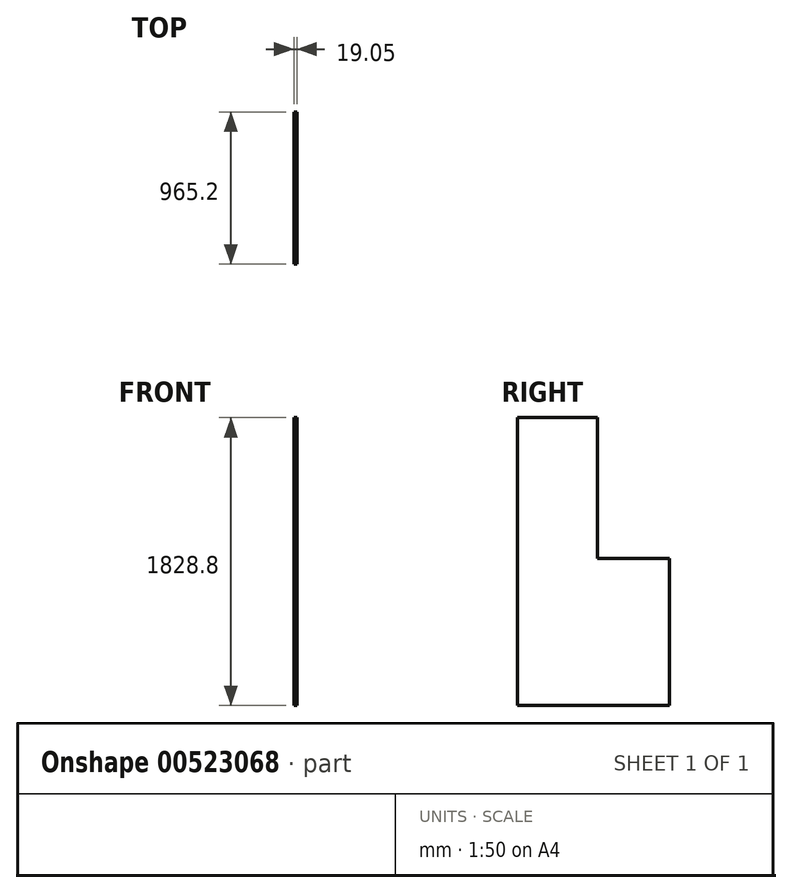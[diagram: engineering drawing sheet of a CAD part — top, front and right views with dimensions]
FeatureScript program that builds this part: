
annotation { "Feature Type Name" : "Feature", "Feature Type Description" : "" }
export const myFeature = defineFeature(function(context is Context, id is Id, definition is map)
    precondition{}
    {
        {
            var Q0;
            Q0=qCreatedBy(makeId("Right.planeOp"),FACE);
            var sketch = newSketch(context, id + "F0", { "sketchPlane" : qUnion([Q0])});
            skLineSegment(sketch, "E0.bottom", {"start": v(0, 0) * mm, "end": v(965.2, 0) * mm});
            skLineSegment(sketch, "E0.top", {"start": v(0, 1828.8) * mm, "end": v(965.2, 1828.8) * mm});
            skLineSegment(sketch, "E0.left", {"start": v(0, 0) * mm, "end": v(0, 1828.8) * mm});
            skLineSegment(sketch, "E0.right", {"start": v(965.2, 0) * mm, "end": v(965.2, 1828.8) * mm});
            skSolve(sketch);
        }
        {
            var Q0;
            Q0 = qSketchRegion(id + "F0", true);
            extrude(context, id + "F1", {"entities" : qUnion([Q0]), "depth" : 19.05 * mm, "offsetDistance" : 25.4 * mm});
        }
        {
            var Q0;
            Q0=makeQuery(id+"F1.opExtrude","CAP_FACE",FACE,{"disambiguationData":[OSD([sQuery(id+"F0.wireOp",EDGE,"E0.bottom"),sQuery(id+"F0.wireOp",EDGE,"E0.top"),sQuery(id+"F0.wireOp",EDGE,"E0.left"),sQuery(id+"F0.wireOp",EDGE,"E0.right")])],"isStart":false});
            var sketch = newSketch(context, id + "F2", { "sketchPlane" : qUnion([Q0])});
            skLineSegment(sketch, "E1.bottom", {"start": v(965.2, 1828.8) * mm, "end": v(508, 1828.8) * mm});
            skLineSegment(sketch, "E1.top", {"start": v(965.2, 933.45) * mm, "end": v(508, 933.45) * mm});
            skLineSegment(sketch, "E1.left", {"start": v(965.2, 1828.8) * mm, "end": v(965.2, 933.45) * mm});
            skLineSegment(sketch, "E1.right", {"start": v(508, 1828.8) * mm, "end": v(508, 933.45) * mm});
            skSolve(sketch);
        }
        {
            var Q0;
            Q0 = qSketchRegion(id + "F2", true);
            extrude(context, id + "F3", {"entities" : qUnion([Q0]), "operationType" : NewBodyOperationType.REMOVE, "endBound" : BoundingType.THROUGH_ALL, "oppositeDirection" : true, "depth" : 25.4 * mm, "offsetDistance" : 25.4 * mm});
        }
    });
